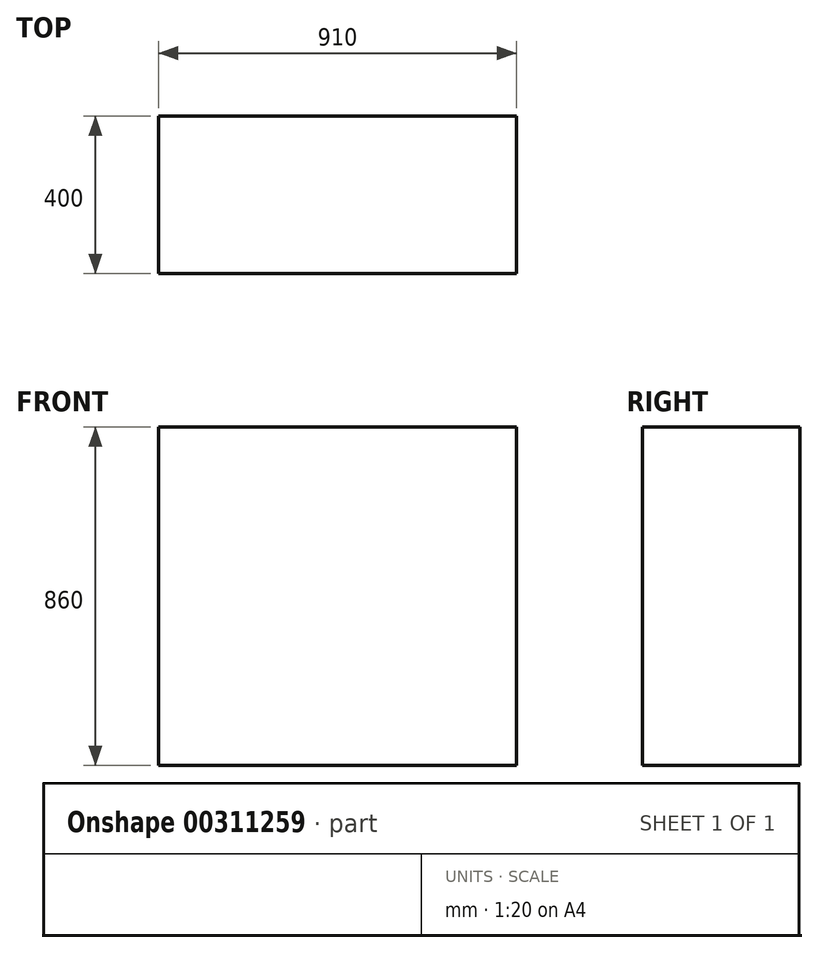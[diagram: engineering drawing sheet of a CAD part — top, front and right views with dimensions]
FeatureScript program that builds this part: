
annotation { "Feature Type Name" : "Feature", "Feature Type Description" : "" }
export const myFeature = defineFeature(function(context is Context, id is Id, definition is map)
    precondition{}
    {
        {
            var Q0;
            Q0=qCreatedBy(makeId("Front.planeOp"),FACE);
            var sketch = newSketch(context, id + "F0", { "sketchPlane" : qUnion([Q0])});
            skLineSegment(sketch, "E0.bottom", {"start": v(0, 0) * mm, "end": v(910, 0) * mm});
            skLineSegment(sketch, "E0.top", {"start": v(0, 860) * mm, "end": v(910, 860) * mm});
            skLineSegment(sketch, "E0.left", {"start": v(0, 0) * mm, "end": v(0, 860) * mm});
            skLineSegment(sketch, "E0.right", {"start": v(910, 0) * mm, "end": v(910, 860) * mm});
            skSolve(sketch);
        }
        {
            var Q0;
            Q0=makeQuery(id+"F0.imprint","IMPRINT",FACE,{"disambiguationData":[TD([[makeQuery(id+"F0.imprint","IMPRINT",EDGE,{"derivedFrom":sQuery(id+"F0.wireOp",EDGE,"E0.bottom")}),1.0]])]});
            extrude(context, id + "F1", {"entities" : qUnion([Q0]), "oppositeDirection" : true, "depth" : 400 * mm});
        }
    });
